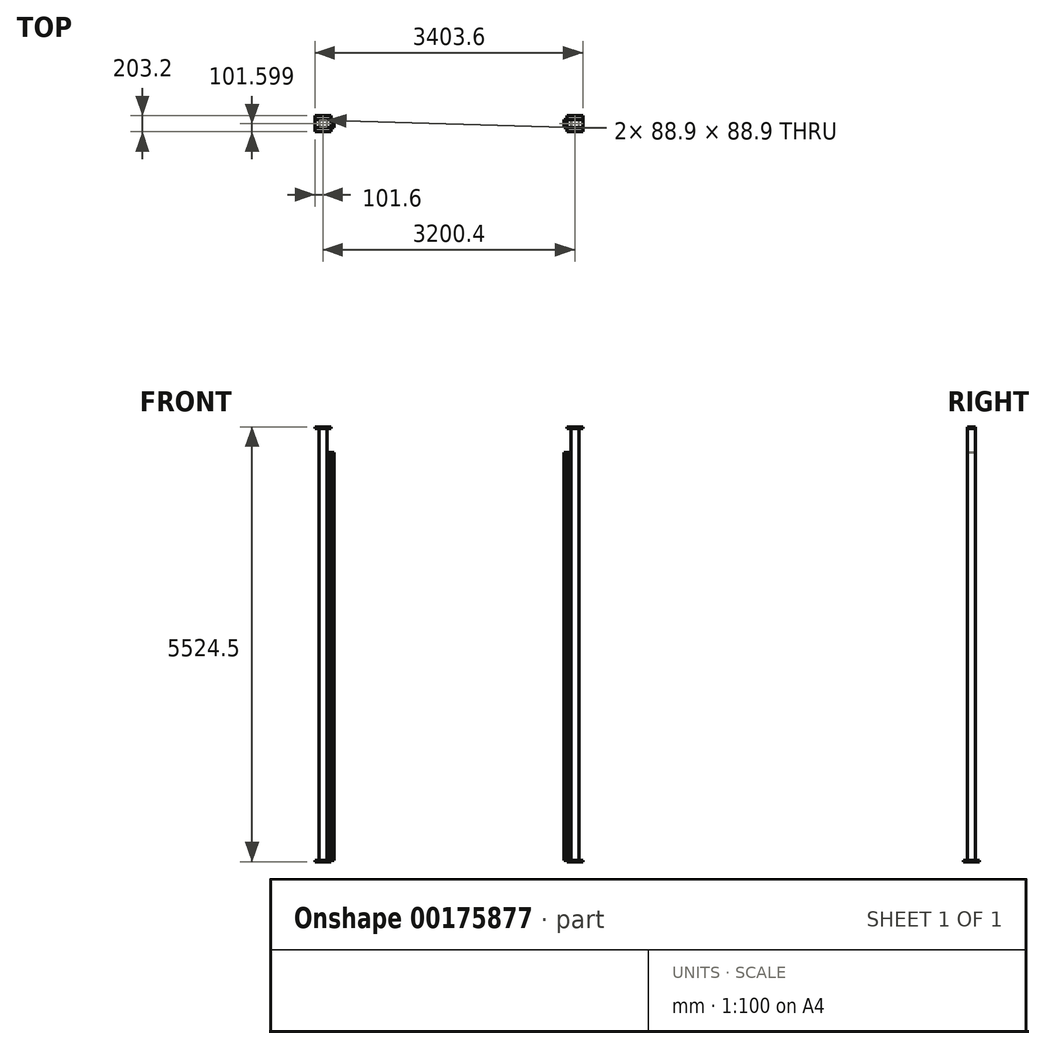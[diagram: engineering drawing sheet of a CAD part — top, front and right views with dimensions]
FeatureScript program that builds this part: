
annotation { "Feature Type Name" : "Feature", "Feature Type Description" : "" }
export const myFeature = defineFeature(function(context is Context, id is Id, definition is map)
    precondition{}
    {
        {
            var Q0;
            Q0=qCreatedBy(makeId("Top.planeOp"),FACE);
            var sketch = newSketch(context, id + "F0", { "sketchPlane" : qUnion([Q0])});
            skPoint(sketch, "E0", {"position": v(-1549.4, 707.9) * mm});
            skLineSegment(sketch, "E1.bottom", {"start": v(-1549.4, 707.9) * mm, "end": v(-1651, 707.9) * mm});
            skLineSegment(sketch, "E1.top", {"start": v(-1549.4, 809.5) * mm, "end": v(-1651, 809.5) * mm});
            skLineSegment(sketch, "E1.left", {"start": v(-1549.4, 707.9) * mm, "end": v(-1549.4, 809.5) * mm});
            skLineSegment(sketch, "E1.right", {"start": v(-1651, 707.9) * mm, "end": v(-1651, 809.5) * mm});
            skLineSegment(sketch, "E2.bottom", {"start": v(-1555.75, 803.15) * mm, "end": v(-1644.65, 803.15) * mm});
            skLineSegment(sketch, "E2.top", {"start": v(-1555.75, 714.25) * mm, "end": v(-1644.65, 714.25) * mm});
            skLineSegment(sketch, "E2.left", {"start": v(-1555.75, 803.15) * mm, "end": v(-1555.75, 714.25) * mm});
            skLineSegment(sketch, "E2.right", {"start": v(-1644.65, 803.15) * mm, "end": v(-1644.65, 714.25) * mm});
            skPoint(sketch, "E2.middle", {"position": v(-1600.2, 758.7) * mm});
            skPoint(sketch, "E2.middle.positionSnap0", {"position": v(-1549.4, 758.7) * mm});
            skPoint(sketch, "E2.middle.positionSnap1", {"position": v(-1600.2, 809.5) * mm});
            skPoint(sketch, "E2.centerSnap0", {"position": v(-1549.4, 758.7) * mm});
            skPoint(sketch, "E2.centerSnap1", {"position": v(-1600.2, 809.5) * mm});
            skLineSegment(sketch, "E3.MirrorCS", {"start": v(1644.65, 803.15) * mm, "end": v(1644.65, 714.25) * mm});
            skLineSegment(sketch, "E4.MirrorCS", {"start": v(1555.75, 803.15) * mm, "end": v(1555.75, 714.25) * mm});
            skLineSegment(sketch, "E5.MirrorCS", {"start": v(1555.75, 714.25) * mm, "end": v(1644.65, 714.25) * mm});
            skLineSegment(sketch, "E6.MirrorCS", {"start": v(1549.4, 809.5) * mm, "end": v(1651, 809.5) * mm});
            skLineSegment(sketch, "E7.MirrorCS", {"start": v(1549.4, 707.9) * mm, "end": v(1549.4, 809.5) * mm});
            skLineSegment(sketch, "E8.MirrorCS", {"start": v(1651, 707.9) * mm, "end": v(1651, 809.5) * mm});
            skLineSegment(sketch, "E9.MirrorCS", {"start": v(1555.75, 803.15) * mm, "end": v(1644.65, 803.15) * mm});
            skLineSegment(sketch, "E10.MirrorCS", {"start": v(1549.4, 707.9) * mm, "end": v(1651, 707.9) * mm});
            skPoint(sketch, "E11.MirrorP", {"position": v(1600.2, 809.5) * mm});
            skPoint(sketch, "E12.MirrorP", {"position": v(1549.4, 758.7) * mm});
            skPoint(sketch, "E13.MirrorP", {"position": v(1549.4, 707.9) * mm});
            skPoint(sketch, "E14.MirrorP", {"position": v(1600.2, 758.7) * mm});
            skSolve(sketch);
        }
        {
            var Q0;
            Q0 = qSketchRegion(id + "F0", true);
            extrude(context, id + "F1", {"entities" : qUnion([Q0]), "depth" : 5486.4 * mm});
        }
        {
            var Q0;
            Q0=makeQuery(id+"F1.opExtrude","CAP_FACE",FACE,{"disambiguationData":[OSD([sQuery(id+"F0.wireOp",EDGE,"E1.bottom"),sQuery(id+"F0.wireOp",EDGE,"E1.top"),sQuery(id+"F0.wireOp",EDGE,"E1.left"),sQuery(id+"F0.wireOp",EDGE,"E1.right"),sQuery(id+"F0.wireOp",EDGE,"E2.bottom"),sQuery(id+"F0.wireOp",EDGE,"E2.top"),sQuery(id+"F0.wireOp",EDGE,"E2.left"),sQuery(id+"F0.wireOp",EDGE,"E2.right")])],"isStart":true});
            var sketch = newSketch(context, id + "F2", { "sketchPlane" : qUnion([Q0])});
            skLineSegment(sketch, "E15.bottom", {"start": v(-1498.6, -860.3) * mm, "end": v(-1701.8, -860.3) * mm});
            skLineSegment(sketch, "E15.top", {"start": v(-1498.6, -657.1) * mm, "end": v(-1701.8, -657.1) * mm});
            skLineSegment(sketch, "E15.left", {"start": v(-1498.6, -860.3) * mm, "end": v(-1498.6, -657.1) * mm});
            skLineSegment(sketch, "E15.right", {"start": v(-1701.8, -860.3) * mm, "end": v(-1701.8, -657.1) * mm});
            skPoint(sketch, "E15.middle", {"position": v(-1600.2, -758.7) * mm});
            skPoint(sketch, "E15.middle.positionSnap0", {"position": v(-1555.75, -758.7) * mm});
            skPoint(sketch, "E15.middle.positionSnap1", {"position": v(-1600.2, -707.9) * mm});
            skPoint(sketch, "E15.centerSnap0", {"position": v(-1555.75, -758.7) * mm});
            skPoint(sketch, "E15.centerSnap1", {"position": v(-1600.2, -707.9) * mm});
            skLineSegment(sketch, "E16.MirrorCS", {"start": v(1498.6, -860.3) * mm, "end": v(1498.6, -657.1) * mm});
            skLineSegment(sketch, "E17.MirrorCS", {"start": v(1498.6, -860.3) * mm, "end": v(1701.8, -860.3) * mm});
            skLineSegment(sketch, "E18.MirrorCS", {"start": v(1701.8, -860.3) * mm, "end": v(1701.8, -657.1) * mm});
            skLineSegment(sketch, "E19.MirrorCS", {"start": v(1498.6, -657.1) * mm, "end": v(1701.8, -657.1) * mm});
            skSolve(sketch);
        }
        {
            var Q0;
            Q0 = qSketchRegion(id + "F2", true);
            extrude(context, id + "F3", {"entities" : qUnion([Q0]), "depth" : 19.05 * mm});
        }
        {
            var Q0;
            Q0=makeQuery(id+"F1.opExtrude","CAP_FACE",FACE,{"disambiguationData":[OSD([sQuery(id+"F0.wireOp",EDGE,"E1.bottom"),sQuery(id+"F0.wireOp",EDGE,"E1.top"),sQuery(id+"F0.wireOp",EDGE,"E1.left"),sQuery(id+"F0.wireOp",EDGE,"E1.right"),sQuery(id+"F0.wireOp",EDGE,"E2.bottom"),sQuery(id+"F0.wireOp",EDGE,"E2.top"),sQuery(id+"F0.wireOp",EDGE,"E2.left"),sQuery(id+"F0.wireOp",EDGE,"E2.right")])],"isStart":false});
            var sketch = newSketch(context, id + "F4", { "sketchPlane" : qUnion([Q0])});
            skLineSegment(sketch, "E20.bottom", {"start": v(-1498.6, 809.5) * mm, "end": v(-1701.8, 809.5) * mm});
            skLineSegment(sketch, "E20.top", {"start": v(-1498.6, 707.9) * mm, "end": v(-1701.8, 707.9) * mm});
            skLineSegment(sketch, "E20.left", {"start": v(-1498.6, 809.5) * mm, "end": v(-1498.6, 707.9) * mm});
            skLineSegment(sketch, "E20.right", {"start": v(-1701.8, 809.5) * mm, "end": v(-1701.8, 707.9) * mm});
            skPoint(sketch, "E20.middle", {"position": v(-1600.2, 758.7) * mm});
            skPoint(sketch, "E20.middle.positionSnap0", {"position": v(-1555.75, 758.7) * mm});
            skPoint(sketch, "E20.middle.positionSnap1", {"position": v(-1600.2, 803.15) * mm});
            skPoint(sketch, "E20.cornerSnap0", {"position": v(-1600.2, 809.5) * mm});
            skPoint(sketch, "E20.centerSnap0", {"position": v(-1555.75, 758.7) * mm});
            skPoint(sketch, "E20.centerSnap1", {"position": v(-1600.2, 803.15) * mm});
            skLineSegment(sketch, "E21.MirrorCS", {"start": v(1498.6, 809.5) * mm, "end": v(1701.8, 809.5) * mm});
            skLineSegment(sketch, "E22.MirrorCS", {"start": v(1498.6, 707.9) * mm, "end": v(1701.8, 707.9) * mm});
            skLineSegment(sketch, "E23.MirrorCS", {"start": v(1498.6, 809.5) * mm, "end": v(1498.6, 707.9) * mm});
            skLineSegment(sketch, "E24.MirrorCS", {"start": v(1701.8, 809.5) * mm, "end": v(1701.8, 707.9) * mm});
            skSolve(sketch);
        }
        {
            var Q0;
            Q0 = qSketchRegion(id + "F4", true);
            extrude(context, id + "F5", {"entities" : qUnion([Q0]), "depth" : 19.05 * mm});
        }
        {
            var Q0;
            Q0=makeQuery(id+"F3.opExtrude","CAP_FACE",FACE,{"disambiguationData":[OSD([sQuery(id+"F2.wireOp",EDGE,"E15.bottom"),sQuery(id+"F2.wireOp",EDGE,"E15.top"),sQuery(id+"F2.wireOp",EDGE,"E15.left"),sQuery(id+"F2.wireOp",EDGE,"E15.right")])],"isStart":true});
            var sketch = newSketch(context, id + "F6", { "sketchPlane" : qUnion([Q0])});
            skLineSegment(sketch, "E25.bottom", {"start": v(-1547.58, 708.74) * mm, "end": v(-1515.47, 708.74) * mm});
            skLineSegment(sketch, "E25.top", {"start": v(-1547.58, 810.34) * mm, "end": v(-1458.68, 810.34) * mm});
            skLineSegment(sketch, "E25.left", {"start": v(-1547.58, 708.74) * mm, "end": v(-1547.58, 810.34) * mm});
            skLineSegment(sketch, "E25.right", {"start": v(-1458.68, 708.74) * mm, "end": v(-1458.68, 810.34) * mm});
            skLineSegment(sketch, "E26.bottom", {"start": v(-1461.35, 807.67) * mm, "end": v(-1544.91, 807.67) * mm});
            skLineSegment(sketch, "E26.top", {"start": v(-1461.35, 711.4) * mm, "end": v(-1490.13, 711.4) * mm});
            skLineSegment(sketch, "E26.left", {"start": v(-1461.35, 807.67) * mm, "end": v(-1461.35, 711.4) * mm});
            skLineSegment(sketch, "E26.right", {"start": v(-1544.91, 807.67) * mm, "end": v(-1544.91, 711.4) * mm});
            skPoint(sketch, "E26.middle", {"position": v(-1503.13, 759.54) * mm});
            skPoint(sketch, "E26.middle.positionSnap0", {"position": v(-1547.58, 759.54) * mm});
            skPoint(sketch, "E26.middle.positionSnap1", {"position": v(-1503.13, 810.34) * mm});
            skPoint(sketch, "E26.centerSnap0", {"position": v(-1547.58, 759.54) * mm});
            skPoint(sketch, "E26.centerSnap1", {"position": v(-1503.13, 810.34) * mm});
            skPoint(sketch, "E27.endSnap0", {"position": v(-1503.13, 711.4) * mm});
            skLineSegment(sketch, "E28", {"start": v(-1490.13, 711.4) * mm, "end": v(-1490.07, 708.74) * mm});
            skLineSegment(sketch, "E29", {"start": v(-1515.47, 708.74) * mm, "end": v(-1515.47, 711.4) * mm});
            skPoint(sketch, "E30.start.orphan", {"position": v(-1503.13, 708.74) * mm});
            skLineSegment(sketch, "E31.trimOffspring", {"start": v(-1490.07, 708.74) * mm, "end": v(-1458.68, 708.74) * mm});
            skLineSegment(sketch, "E32.trimOffspring", {"start": v(-1515.47, 711.4) * mm, "end": v(-1544.91, 711.4) * mm});
            skPoint(sketch, "E27.start.orphan", {"position": v(-1503.13, 711.4) * mm});
            skLineSegment(sketch, "E33.MirrorCS", {"start": v(1490.13, 711.4) * mm, "end": v(1490.07, 708.74) * mm});
            skLineSegment(sketch, "E34.MirrorCS", {"start": v(1515.47, 708.74) * mm, "end": v(1515.47, 711.4) * mm});
            skLineSegment(sketch, "E35.MirrorCS", {"start": v(1515.47, 711.4) * mm, "end": v(1544.91, 711.4) * mm});
            skLineSegment(sketch, "E36.MirrorCS", {"start": v(1490.07, 708.74) * mm, "end": v(1458.68, 708.74) * mm});
            skLineSegment(sketch, "E37.MirrorCS", {"start": v(1544.91, 807.67) * mm, "end": v(1544.91, 711.4) * mm});
            skLineSegment(sketch, "E38.MirrorCS", {"start": v(1461.35, 711.4) * mm, "end": v(1490.13, 711.4) * mm});
            skLineSegment(sketch, "E39.MirrorCS", {"start": v(1461.35, 807.67) * mm, "end": v(1544.91, 807.67) * mm});
            skLineSegment(sketch, "E40.MirrorCS", {"start": v(1547.58, 708.74) * mm, "end": v(1547.58, 810.34) * mm});
            skPoint(sketch, "E41.MirrorP", {"position": v(1503.13, 711.4) * mm});
            skLineSegment(sketch, "E42.MirrorCS", {"start": v(1547.58, 810.34) * mm, "end": v(1458.68, 810.34) * mm});
            skLineSegment(sketch, "E43.MirrorCS", {"start": v(1547.58, 708.74) * mm, "end": v(1515.47, 708.74) * mm});
            skPoint(sketch, "E44.MirrorP", {"position": v(1503.13, 810.34) * mm});
            skPoint(sketch, "E45.MirrorP", {"position": v(1547.58, 759.54) * mm});
            skLineSegment(sketch, "E46.MirrorCS", {"start": v(1458.68, 708.74) * mm, "end": v(1458.68, 810.34) * mm});
            skLineSegment(sketch, "E47.MirrorCS", {"start": v(1461.35, 807.67) * mm, "end": v(1461.35, 711.4) * mm});
            skPoint(sketch, "E48.MirrorP", {"position": v(1503.13, 708.74) * mm});
            skPoint(sketch, "E49.MirrorP", {"position": v(1503.13, 759.54) * mm});
            skSolve(sketch);
        }
        {
            var Q0;
            Q0 = qSketchRegion(id + "F6", true);
            extrude(context, id + "F7", {"entities" : qUnion([Q0]), "depth" : 5181.6 * mm});
        }
    });
